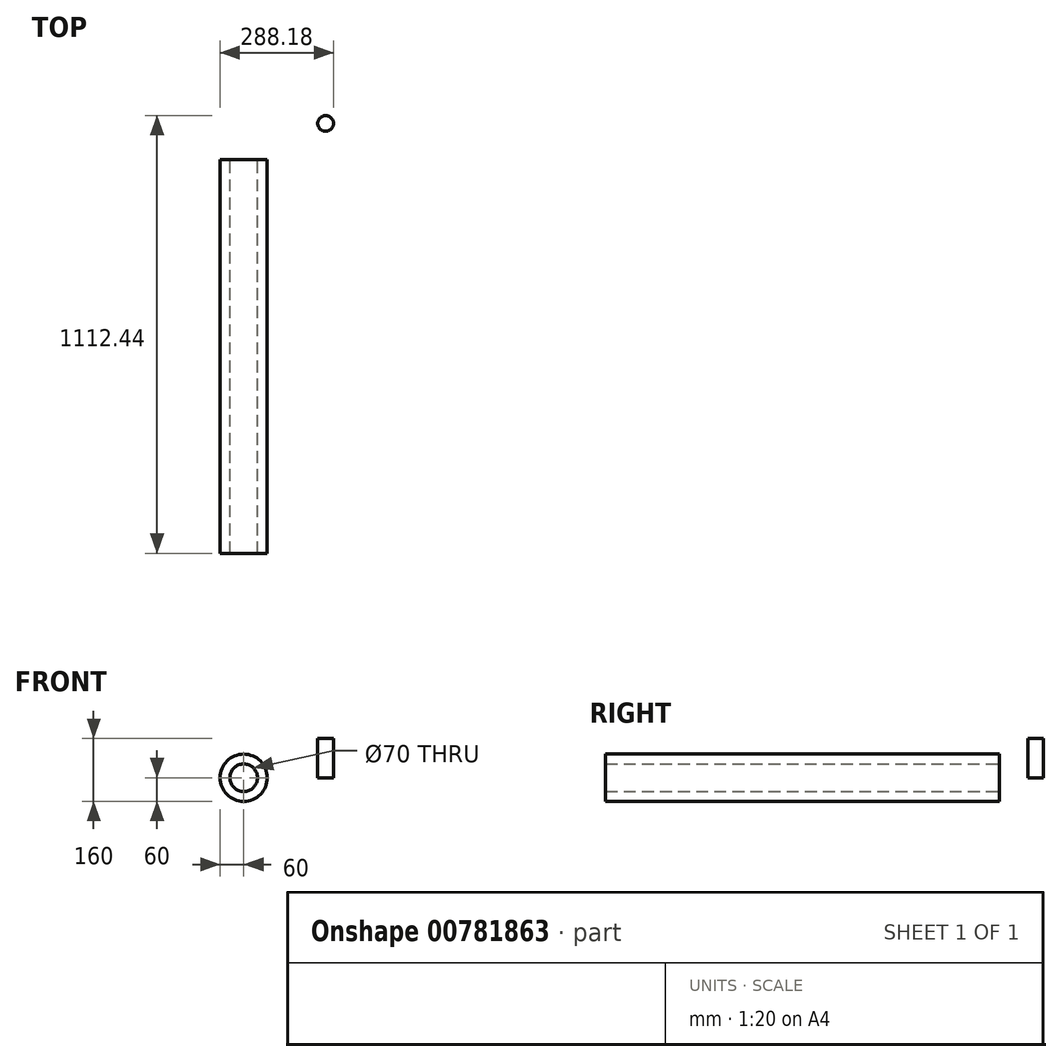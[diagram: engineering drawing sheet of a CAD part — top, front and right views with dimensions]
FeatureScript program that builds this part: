
annotation { "Feature Type Name" : "Feature", "Feature Type Description" : "" }
export const myFeature = defineFeature(function(context is Context, id is Id, definition is map)
    precondition{}
    {
        {
            var Q0;
            Q0=qCreatedBy(makeId("Front.planeOp"),FACE);
            var sketch = newSketch(context, id + "F0", { "sketchPlane" : qUnion([Q0])});
            skCircle(sketch, "E0", {"center": v(0, 0) * mm, "radius": 60 * mm});
            skCircle(sketch, "E1", {"center": v(0, 0) * mm, "radius": 35 * mm});
            skSolve(sketch);
        }
        {
            var Q0;
            Q0=makeQuery(id+"F0.imprint","IMPRINT",FACE,{"disambiguationData":[TD([[makeQuery(id+"F0.imprint","IMPRINT",EDGE,{"derivedFrom":sQuery(id+"F0.wireOp",EDGE,"E0")}),1.0]])]});
            extrude(context, id + "F1", {"entities" : qUnion([Q0]), "depth" : 1000 * mm, "offsetDistance" : 25 * mm});
        }
        {
            var Q0;
            Q0=qCreatedBy(makeId("Top.planeOp"),FACE);
            var sketch = newSketch(context, id + "F2", { "sketchPlane" : qUnion([Q0])});
            skCircle(sketch, "E2", {"center": v(208.18, 92.44) * mm, "radius": 20 * mm});
            skSolve(sketch);
        }
        {
            var Q0;
            Q0=makeQuery(id+"F2.imprint","IMPRINT",FACE,{"disambiguationData":[TD([[makeQuery(id+"F2.imprint","IMPRINT",EDGE,{"derivedFrom":sQuery(id+"F2.wireOp",EDGE,"E2")}),1.0]])]});
            extrude(context, id + "F3", {"entities" : qUnion([Q0]), "depth" : 100 * mm, "offsetDistance" : 25 * mm});
        }
    });
